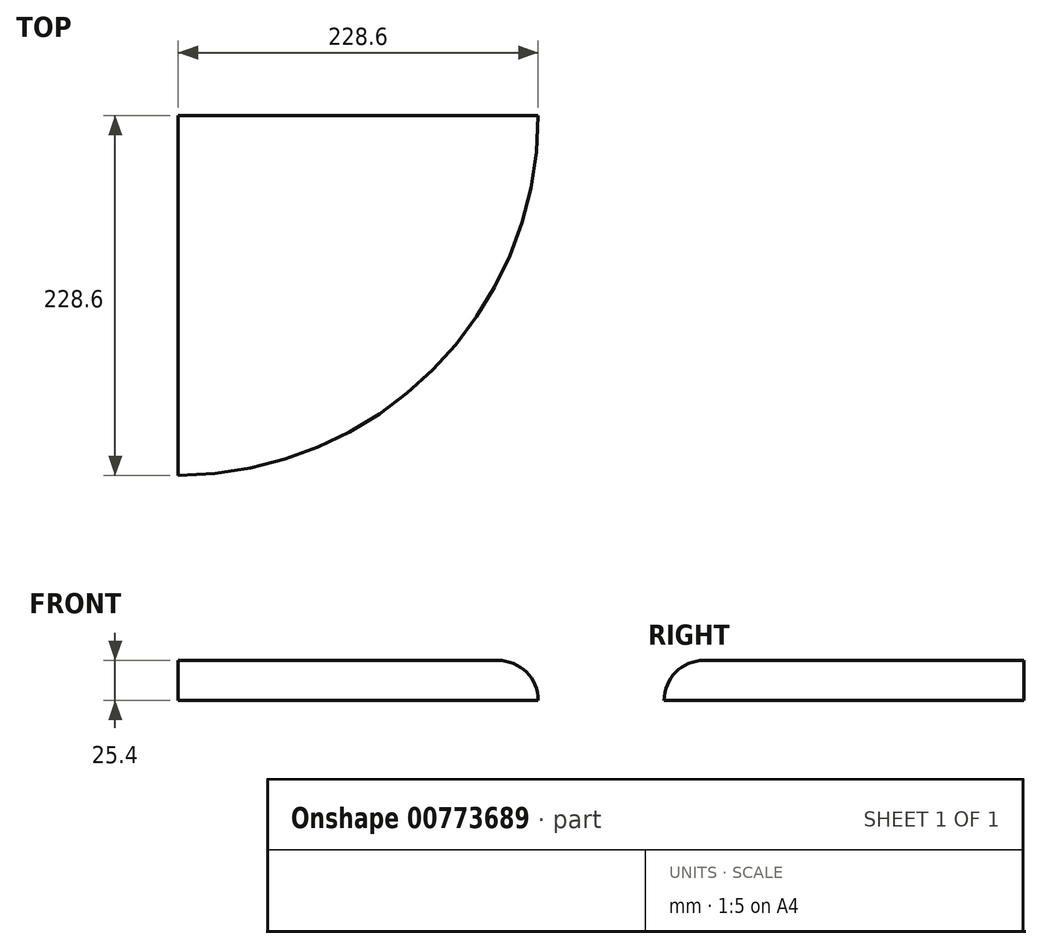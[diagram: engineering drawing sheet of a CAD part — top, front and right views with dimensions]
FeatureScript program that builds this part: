
annotation { "Feature Type Name" : "Feature", "Feature Type Description" : "" }
export const myFeature = defineFeature(function(context is Context, id is Id, definition is map)
    precondition{}
    {
        {
            var Q0;
            Q0=qCreatedBy(makeId("Top.planeOp"),FACE);
            var sketch = newSketch(context, id + "F0", { "sketchPlane" : qUnion([Q0])});
            skCircle(sketch, "E0", {"center": v(0, 0) * mm, "radius": 228.6 * mm});
            skSolve(sketch);
        }
        {
            var Q0;
            Q0=makeQuery(id+"F0.imprint","IMPRINT",FACE,{"disambiguationData":[TD([[makeQuery(id+"F0.imprint","IMPRINT",EDGE,{"derivedFrom":sQuery(id+"F0.wireOp",EDGE,"E0")}),1.0]])]});
            var sketch = newSketch(context, id + "F1", { "sketchPlane" : qUnion([Q0])});
            skLineSegment(sketch, "E1", {"start": v(0, 0) * mm, "end": v(0, 228.6) * mm});
            skLineSegment(sketch, "E2", {"start": v(0, 0) * mm, "end": v(228.6, 0) * mm});
            skLineSegment(sketch, "E3", {"start": v(0, 228.6) * mm, "end": v(0, -228.6) * mm});
            skLineSegment(sketch, "E4", {"start": v(228.6, 0) * mm, "end": v(-228.6, 0) * mm});
            skLineSegment(sketch, "E5", {"start": v(0, 0) * mm, "end": v(161.64, 161.64) * mm});
            skLineSegment(sketch, "E6.0", {"start": v(20.2, -20.2) * mm, "end": v(181.85, 141.44) * mm});
            skLineSegment(sketch, "E7.0", {"start": v(40.41, -40.41) * mm, "end": v(202.06, 121.23) * mm});
            skLineSegment(sketch, "E8.0", {"start": v(60.62, -60.62) * mm, "end": v(222.26, 101.03) * mm});
            skLineSegment(sketch, "E9.0", {"start": v(80.82, -80.82) * mm, "end": v(242.47, 80.82) * mm});
            skLineSegment(sketch, "E10.0", {"start": v(101.03, -101.03) * mm, "end": v(262.67, 60.62) * mm});
            skLineSegment(sketch, "E11.0", {"start": v(-20.2, 20.2) * mm, "end": v(141.44, 181.85) * mm});
            skLineSegment(sketch, "E12.0", {"start": v(-40.41, 40.41) * mm, "end": v(121.23, 202.06) * mm});
            skLineSegment(sketch, "E13.0", {"start": v(-60.62, 60.62) * mm, "end": v(101.03, 222.26) * mm});
            skLineSegment(sketch, "E14.0", {"start": v(-80.82, 80.82) * mm, "end": v(80.82, 242.47) * mm});
            skLineSegment(sketch, "E15.0", {"start": v(-101.03, 101.03) * mm, "end": v(60.62, 262.67) * mm});
            skCircle(sketch, "E16", {"center": v(0, 0) * mm, "radius": 228.6 * mm});
            skSolve(sketch);
        }
        {
            var Q0;
            {var subQ0=sQuery(id+"F1.wireOp",EDGE,"E16");var subQ1=sQuery(id+"F1.wireOp",EDGE,"E3");var subQ2=makeQuery(id+"F1.imprint","INTERSECT",VERTEX,{"disambiguationData":[OD(0.0)],"derivedFrom":[subQ1,subQ0]});Q0=makeQuery(id+"F1.imprint","IMPRINT",FACE,{"disambiguationData":[TD([[makeQuery(id+"F1.imprint","IMPRINT",EDGE,{"disambiguationData":[TD([[subQ2,-1.0]])],"derivedFrom":subQ1}),1.0]])]});}
            extrude(context, id + "F2", {"entities" : qUnion([Q0]), "depth" : 25.4 * mm, "offsetDistance" : 25.4 * mm});
        }
        {
            var Q0;
            Q0=makeQuery(id+"F2.opExtrude","CAP_EDGE",EDGE,{"disambiguationData":[OSD([sQuery(id+"F1.wireOp",EDGE,"E16")])],"isStart":false});
            fillet(context, id + "F3", {"entities" : qUnion([Q0]), "radius" : 25.4 * mm, "tangentPropagation" : true, "allowEdgeOverflow" : false});
        }
    });
